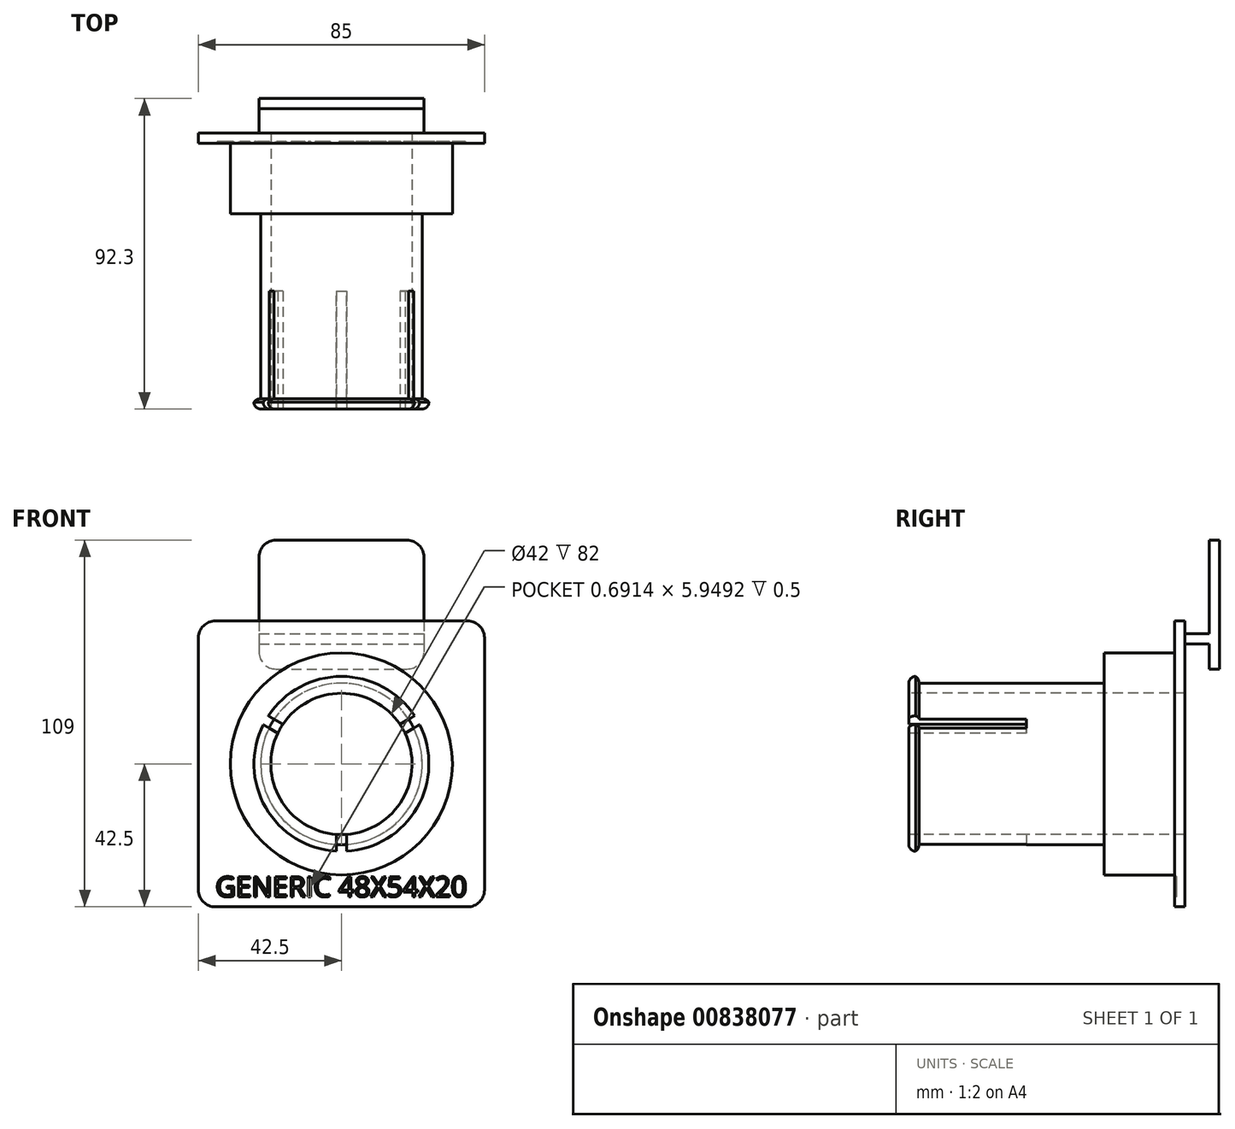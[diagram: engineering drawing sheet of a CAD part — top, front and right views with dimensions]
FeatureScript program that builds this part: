
annotation { "Feature Type Name" : "Feature", "Feature Type Description" : "" }
export const myFeature = defineFeature(function(context is Context, id is Id, definition is map)
    precondition{}
    {
        {
            assignVariable(context, id + "F0", {"name" : "BaseRingHeight", "anyValue" : 21});
        }
        {
            assignVariable(context, id + "F1", {"name" : "SpoolRingHeight", "anyValue" : 55});
        }
        {
            var Q0;
            Q0=qCreatedBy(makeId("Front.planeOp"),FACE);
            var sketch = newSketch(context, id + "F2", { "sketchPlane" : qUnion([Q0])});
            skLineSegment(sketch, "E0.bottom", {"start": v(-44, 38.3) * mm, "end": v(-5, 38.3) * mm});
            skLineSegment(sketch, "E0.top", {"start": v(-44, 0) * mm, "end": v(-5, 0) * mm});
            skLineSegment(sketch, "E0.left", {"start": v(-49, 33.3) * mm, "end": v(-49, 5) * mm});
            skLineSegment(sketch, "E0.right", {"start": v(0, 33.3) * mm, "end": v(0, 5) * mm});
            skPoint(sketch, "E1.visualSharp", {"position": v(-49, 38.3) * mm});
            skArc(sketch, "E1.filletArc", {"start": v(-44, 38.3) * mm, "mid": v(-47.54, 36.84) * mm, "end": v(-49, 33.3) * mm});
            skPoint(sketch, "E2.visualSharp", {"position": v(0, 38.3) * mm});
            skArc(sketch, "E2.filletArc", {"start": v(0, 33.3) * mm, "mid": v(-1.46, 36.84) * mm, "end": v(-5, 38.3) * mm});
            skPoint(sketch, "E3.visualSharp", {"position": v(0, 0) * mm});
            skArc(sketch, "E3.filletArc", {"start": v(-5, 0) * mm, "mid": v(-1.46, 1.46) * mm, "end": v(0, 5) * mm});
            skPoint(sketch, "E4.visualSharp", {"position": v(-49, 0) * mm});
            skArc(sketch, "E4.filletArc", {"start": v(-49, 5) * mm, "mid": v(-47.54, 1.46) * mm, "end": v(-44, 0) * mm});
            skSolve(sketch);
        }
        {
            var Q0;
            Q0=qSketchRegion(id+"F2",true);
            extrude(context, id + "F3", {"entities" : qUnion([Q0]), "depth" : 3 * mm, "offsetDistance" : 25 * mm});
        }
        {
            var Q0;
            Q0=makeQuery(id+"F3.opExtrude","CAP_FACE",FACE,{"disambiguationData":[OSD([sQuery(id+"F2.wireOp",EDGE,"E0.bottom"),sQuery(id+"F2.wireOp",EDGE,"E0.top"),sQuery(id+"F2.wireOp",EDGE,"E0.left"),sQuery(id+"F2.wireOp",EDGE,"E0.right")])],"isStart":false});
            var sketch = newSketch(context, id + "F4", { "sketchPlane" : qUnion([Q0])});
            skLineSegment(sketch, "E5.bottom", {"start": v(-49, 10.5) * mm, "end": v(0, 10.5) * mm});
            skLineSegment(sketch, "E5.top", {"start": v(-49, 7.5) * mm, "end": v(0, 7.5) * mm});
            skLineSegment(sketch, "E5.left", {"start": v(-49, 10.5) * mm, "end": v(-49, 7.5) * mm});
            skLineSegment(sketch, "E5.right", {"start": v(0, 10.5) * mm, "end": v(0, 7.5) * mm});
            skSolve(sketch);
        }
        {
            var Q0;
            Q0=qSketchRegion(id+"F4",true);
            extrude(context, id + "F5", {"entities" : qUnion([Q0]), "operationType" : NewBodyOperationType.ADD, "depth" : 7.3 * mm, "offsetDistance" : 25 * mm});
        }
        {
            var Q0;
            Q0=makeQuery(id+"F5.opExtrude","CAP_FACE",FACE,{"disambiguationData":[OSD([sQuery(id+"F4.wireOp",EDGE,"E5.bottom"),sQuery(id+"F4.wireOp",EDGE,"E5.top"),sQuery(id+"F4.wireOp",EDGE,"E5.left"),sQuery(id+"F4.wireOp",EDGE,"E5.right")])],"isStart":false});
            var sketch = newSketch(context, id + "F6", { "sketchPlane" : qUnion([Q0])});
            skLineSegment(sketch, "E6.bottom", {"start": v(-62, 14.3) * mm, "end": v(13, 14.3) * mm});
            skLineSegment(sketch, "E6.top", {"start": v(-62, -70.7) * mm, "end": v(13, -70.7) * mm});
            skLineSegment(sketch, "E6.left", {"start": v(-67, 9.3) * mm, "end": v(-67, -65.7) * mm});
            skLineSegment(sketch, "E6.right", {"start": v(18, 9.3) * mm, "end": v(18, -65.7) * mm});
            skPoint(sketch, "E7.visualSharp", {"position": v(-67, 14.3) * mm});
            skArc(sketch, "E7.filletArc", {"start": v(-62, 14.3) * mm, "mid": v(-65.54, 12.84) * mm, "end": v(-67, 9.3) * mm});
            skPoint(sketch, "E8.visualSharp", {"position": v(18, 14.3) * mm});
            skArc(sketch, "E8.filletArc", {"start": v(18, 9.3) * mm, "mid": v(16.54, 12.84) * mm, "end": v(13, 14.3) * mm});
            skPoint(sketch, "E9.visualSharp", {"position": v(18, -70.7) * mm});
            skArc(sketch, "E9.filletArc", {"start": v(13, -70.7) * mm, "mid": v(16.54, -69.24) * mm, "end": v(18, -65.7) * mm});
            skPoint(sketch, "E10.visualSharp", {"position": v(-67, -70.7) * mm});
            skArc(sketch, "E10.filletArc", {"start": v(-67, -65.7) * mm, "mid": v(-65.54, -69.24) * mm, "end": v(-62, -70.7) * mm});
            skSolve(sketch);
        }
        {
            var Q0;
            Q0=qSketchRegion(id+"F6",true);
            extrude(context, id + "F7", {"entities" : qUnion([Q0]), "operationType" : NewBodyOperationType.ADD, "depth" : 3 * mm, "offsetDistance" : 25 * mm});
        }
        {
            var Q0;
            Q0=makeQuery(id+"F7.opExtrude","CAP_FACE",FACE,{"disambiguationData":[OSD([sQuery(id+"F6.wireOp",EDGE,"E6.bottom"),sQuery(id+"F6.wireOp",EDGE,"E6.top"),sQuery(id+"F6.wireOp",EDGE,"E6.left"),sQuery(id+"F6.wireOp",EDGE,"E6.right"),sQuery(id+"F6.wireOp",EDGE,"E7.filletArc"),sQuery(id+"F6.wireOp",EDGE,"E8.filletArc"),sQuery(id+"F6.wireOp",EDGE,"E9.filletArc"),sQuery(id+"F6.wireOp",EDGE,"E10.filletArc")])],"isStart":false});
            var sketch = newSketch(context, id + "F8", { "sketchPlane" : qUnion([Q0])});
            skCircle(sketch, "E11", {"center": v(-24.5, -28.2) * mm, "radius": 33 * mm});
            skLineSegment(sketch, "E12", {"start": v(-82.43, -28.2) * mm, "end": v(118.43, -28.2) * mm, "construction": true});
            skLineSegment(sketch, "E13", {"start": v(-24.5, 43.68) * mm, "end": v(-24.5, -185.08) * mm, "construction": true});
            skSolve(sketch);
        }
        {
            var Q0;
            Q0=qSketchRegion(id+"F8",true);
            extrude(context, id + "F9", {"entities" : qUnion([Q0]), "operationType" : NewBodyOperationType.ADD, "depth" : (getVariable(context, 'BaseRingHeight')) * mm, "offsetDistance" : 25 * mm});
        }
        {
            var Q0;
            Q0=makeQuery(id+"F9.opExtrude","CAP_FACE",FACE,{"disambiguationData":[OSD([sQuery(id+"F8.wireOp",EDGE,"E11")])],"isStart":false});
            var sketch = newSketch(context, id + "F10", { "sketchPlane" : qUnion([Q0])});
            skCircle(sketch, "E14", {"center": v(-24.5, -28.2) * mm, "radius": 24 * mm});
            skSolve(sketch);
        }
        {
            var Q0;
            Q0=qSketchRegion(id+"F10",true);
            var Q1;
            Q1=qSketchRegion(id+"F12",true);
            extrude(context, id + "F11", {"entities" : qUnion([Q0, Q1]), "operationType" : NewBodyOperationType.ADD, "depth" : (getVariable(context, 'SpoolRingHeight')) * mm, "offsetDistance" : 25 * mm});
        }
        {
            var Q0;
            Q0=makeQuery(id+"F11.opExtrude","CAP_FACE",FACE,{"disambiguationData":[OSD([sQuery(id+"F10.wireOp",EDGE,"E14")])],"isStart":false});
            var sketch = newSketch(context, id + "F12", { "sketchPlane" : qUnion([Q0])});
            skCircle(sketch, "E15", {"center": v(-24.5, -28.2) * mm, "radius": 21 * mm});
            skSolve(sketch);
        }
        {
            var Q0;
            Q0=qSketchRegion(id+"F12",true);
            var Q1;
            Q1=makeQuery(id+"F7.opExtrude","CAP_FACE",FACE,{"disambiguationData":[OSD([sQuery(id+"F6.wireOp",EDGE,"E6.bottom"),sQuery(id+"F6.wireOp",EDGE,"E6.top"),sQuery(id+"F6.wireOp",EDGE,"E6.left"),sQuery(id+"F6.wireOp",EDGE,"E6.right"),sQuery(id+"F6.wireOp",EDGE,"E7.filletArc"),sQuery(id+"F6.wireOp",EDGE,"E8.filletArc"),sQuery(id+"F6.wireOp",EDGE,"E9.filletArc"),sQuery(id+"F6.wireOp",EDGE,"E10.filletArc")])],"isStart":true});
            extrude(context, id + "F13", {"entities" : qUnion([Q0]), "operationType" : NewBodyOperationType.REMOVE, "endBound" : BoundingType.UP_TO_SURFACE, "oppositeDirection" : true, "depth" : 25 * mm, "endBoundEntityFace" : qUnion([Q1]), "offsetDistance" : 25 * mm});
        }
        {
            var Q0;
            {var subQ0=sQuery(id+"F10.wireOp",EDGE,"E14");Q0=makeQuery(id+"F17.boolean.opBoolean","SPLIT",FACE,{"disambiguationData":[TD([makeQuery(id+"F17.opExtrude","SWEPT_FACE",FACE,{"disambiguationData":[OSD([sQuery(id+"F16.wireOp",EDGE,"E21.left")])]})])],"derivedFrom":makeQuery(id+"F11.opExtrude","CAP_FACE",FACE,{"disambiguationData":[OSD([subQ0])],"isStart":false})});}
            var sketch = newSketch(context, id + "F14", { "sketchPlane" : qUnion([Q0])});
            skCircle(sketch, "E16", {"center": v(-24.5, -28.2) * mm, "radius": 21 * mm});
            skCircle(sketch, "E17", {"center": v(-24.5, -28.2) * mm, "radius": 26 * mm});
            skSolve(sketch);
        }
        {
            var Q0;
            Q0=qSketchRegion(id+"F14",true);
            extrude(context, id + "F15", {"entities" : qUnion([Q0]), "operationType" : NewBodyOperationType.ADD, "depth" : 3 * mm, "offsetDistance" : 25 * mm});
        }
        {
            var Q0;
            Q0=makeQuery(id+"F15.opExtrude","CAP_FACE",FACE,{"disambiguationData":[OSD([sQuery(id+"F14.wireOp",EDGE,"E16"),sQuery(id+"F14.wireOp",EDGE,"E17")])],"isStart":false});
            var sketch = newSketch(context, id + "F16", { "sketchPlane" : qUnion([Q0])});
            skLineSegment(sketch, "E18", {"start": v(-24.5, -28.2) * mm, "end": v(-51, -12.9) * mm, "construction": true});
            skLineSegment(sketch, "E19", {"start": v(-24.5, -28.2) * mm, "end": v(2, -12.9) * mm, "construction": true});
            skLineSegment(sketch, "E20", {"start": v(-24.5, -28.2) * mm, "end": v(-24.5, -58.8) * mm, "construction": true});
            skLineSegment(sketch, "E21.bottom", {"start": v(-26, -28.2) * mm, "end": v(-23, -28.2) * mm});
            skLineSegment(sketch, "E21.top", {"start": v(-26, -58.76) * mm, "end": v(-23, -58.76) * mm});
            skLineSegment(sketch, "E21.left", {"start": v(-26, -28.2) * mm, "end": v(-26, -58.76) * mm});
            skLineSegment(sketch, "E21.right", {"start": v(-23, -28.2) * mm, "end": v(-23, -58.76) * mm});
            skCircle(sketch, "E22", {"center": v(-24.5, -28.2) * mm, "radius": 30.6 * mm, "construction": true});
            skLineSegment(sketch, "E23", {"start": v(1.22, -11.62) * mm, "end": v(2.72, -14.22) * mm});
            skLineSegment(sketch, "E24", {"start": v(2.72, -14.22) * mm, "end": v(-23.75, -29.5) * mm});
            skLineSegment(sketch, "E25", {"start": v(-23.75, -29.5) * mm, "end": v(-25.25, -26.9) * mm});
            skLineSegment(sketch, "E26", {"start": v(-25.25, -26.9) * mm, "end": v(1.22, -11.62) * mm});
            skLineSegment(sketch, "E27", {"start": v(-50.22, -11.62) * mm, "end": v(-51.72, -14.22) * mm});
            skLineSegment(sketch, "E28", {"start": v(-51.72, -14.22) * mm, "end": v(-25.25, -29.5) * mm});
            skLineSegment(sketch, "E29", {"start": v(-25.25, -29.5) * mm, "end": v(-23.75, -26.9) * mm});
            skLineSegment(sketch, "E30", {"start": v(-23.75, -26.9) * mm, "end": v(-50.22, -11.62) * mm});
            skSolve(sketch);
        }
        {
            var Q0;
            Q0=qSketchRegion(id+"F16",true);
            extrude(context, id + "F17", {"entities" : qUnion([Q0]), "operationType" : NewBodyOperationType.REMOVE, "oppositeDirection" : true, "depth" : 70 * mm, "offsetDistance" : 25 * mm, "symmetric" : true});
        }
        {
            var Q0;
            {var subQ0=sQuery(id+"F14.wireOp",EDGE,"E17");Q0=makeQuery(id+"F17.boolean.opBoolean","SPLIT",EDGE,{"disambiguationData":[TD([makeQuery(id+"F17.opExtrude","SWEPT_FACE",FACE,{"disambiguationData":[OSD([sQuery(id+"F16.wireOp",EDGE,"E21.left")])]})])],"derivedFrom":makeQuery(id+"F15.opExtrude","CAP_EDGE",EDGE,{"disambiguationData":[OSD([subQ0])],"isStart":false})});}
            var Q1;
            {var subQ0=sQuery(id+"F14.wireOp",EDGE,"E17");Q1=makeQuery(id+"F17.boolean.opBoolean","SPLIT",EDGE,{"disambiguationData":[TD([makeQuery(id+"F17.opExtrude","SWEPT_FACE",FACE,{"disambiguationData":[OSD([sQuery(id+"F16.wireOp",EDGE,"E26")])]})])],"derivedFrom":makeQuery(id+"F15.opExtrude","CAP_EDGE",EDGE,{"disambiguationData":[OSD([subQ0])],"isStart":false})});}
            var Q2;
            {var subQ0=sQuery(id+"F14.wireOp",EDGE,"E17");Q2=makeQuery(id+"F17.boolean.opBoolean","SPLIT",EDGE,{"disambiguationData":[TD([makeQuery(id+"F17.opExtrude","SWEPT_FACE",FACE,{"disambiguationData":[OSD([sQuery(id+"F16.wireOp",EDGE,"E21.right")])]})])],"derivedFrom":makeQuery(id+"F15.opExtrude","CAP_EDGE",EDGE,{"disambiguationData":[OSD([subQ0])],"isStart":false})});}
            fillet(context, id + "F18", {"entities" : qUnion([Q0, Q1, Q2]), "radius" : 2 * mm, "tangentPropagation" : true, "allowEdgeOverflow" : false});
        }
        {
            var Q0;
            {var subQ0=sQuery(id+"F14.wireOp",EDGE,"E17");Q0=makeQuery(id+"F17.boolean.opBoolean","SPLIT",EDGE,{"disambiguationData":[TD([makeQuery(id+"F17.opExtrude","SWEPT_FACE",FACE,{"disambiguationData":[OSD([sQuery(id+"F16.wireOp",EDGE,"E21.right")])]})])],"derivedFrom":makeQuery(id+"F15.opExtrude","CAP_EDGE",EDGE,{"disambiguationData":[OSD([subQ0])],"isStart":true})});}
            var Q1;
            {var subQ0=sQuery(id+"F14.wireOp",EDGE,"E17");Q1=makeQuery(id+"F17.boolean.opBoolean","SPLIT",EDGE,{"disambiguationData":[TD([makeQuery(id+"F17.opExtrude","SWEPT_FACE",FACE,{"disambiguationData":[OSD([sQuery(id+"F16.wireOp",EDGE,"E26")])]})])],"derivedFrom":makeQuery(id+"F15.opExtrude","CAP_EDGE",EDGE,{"disambiguationData":[OSD([subQ0])],"isStart":true})});}
            var Q2;
            {var subQ0=sQuery(id+"F14.wireOp",EDGE,"E17");Q2=makeQuery(id+"F17.boolean.opBoolean","SPLIT",EDGE,{"disambiguationData":[TD([makeQuery(id+"F17.opExtrude","SWEPT_FACE",FACE,{"disambiguationData":[OSD([sQuery(id+"F16.wireOp",EDGE,"E21.left")])]})])],"derivedFrom":makeQuery(id+"F15.opExtrude","CAP_EDGE",EDGE,{"disambiguationData":[OSD([subQ0])],"isStart":true})});}
            fillet(context, id + "F19", {"entities" : qUnion([Q0, Q1, Q2]), "radius" : 2 * mm, "tangentPropagation" : true, "allowEdgeOverflow" : false});
        }
        {
            var Q0;
            Q0=makeQuery(id+"F8.imprint","IMPRINT",FACE,{"disambiguationData":[TD([[makeQuery(id+"F8.imprint","IMPRINT",EDGE,{"derivedFrom":sQuery(id+"F8.wireOp",EDGE,"E11")}),-1.0]])]});
            var sketch = newSketch(context, id + "F20", { "sketchPlane" : qUnion([Q0])});
            skText(sketch, "E31", { "text": "GENERIC 48X54X20", "fontName": "OpenSans-Regular.ttf"});
            skLineSegment(sketch, "E32", {"start": v(14.01, -67.7) * mm, "end": v(-56.31, -67.7) * mm, "construction": true});
            const initialGuessF20  = {"E31": [-0.06192, -0.0677, 1, 0, 0.006]};
            skSetInitialGuess(sketch, initialGuessF20);
            skSolve(sketch);
        }
        {
            var Q0;
            Q0=qSketchRegion(id+"F20",true);
            extrude(context, id + "F21", {"entities" : qUnion([Q0]), "operationType" : NewBodyOperationType.REMOVE, "oppositeDirection" : true, "depth" : .5 * mm, "offsetDistance" : 25 * mm});
        }
    });
